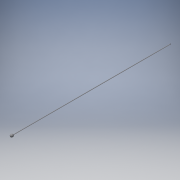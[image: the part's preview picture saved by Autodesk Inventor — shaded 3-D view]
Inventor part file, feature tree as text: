
AUTODESK INVENTOR PART (.ipt)
format: ipt  version: 2018 (Build 220112000, 112)  size: 164,864 bytes
history: native  units: in
note: dims shown in document units (in); Inventor stores cm internally (conversion verified against a paired STEP export)
features: extrude x1, other x1, sketch x1
ambient origin geometry x8: Origin, YZ Plane, XZ Plane, XY Plane, X Axis, Y Axis, Z Axis, Center Point
bodies: Solid1 (feature_tree), Solid3 (feature_tree)
feature tree (3):
  extrude  "Extrusion1"  Depth=5230.5in TaperAngle=0.0deg
  other  "Form2"
  sketch  "Sketch1"  dims[d0=20.0in d1=376.25in d2=5230.5in d3=0.0in d4=0.0in]
